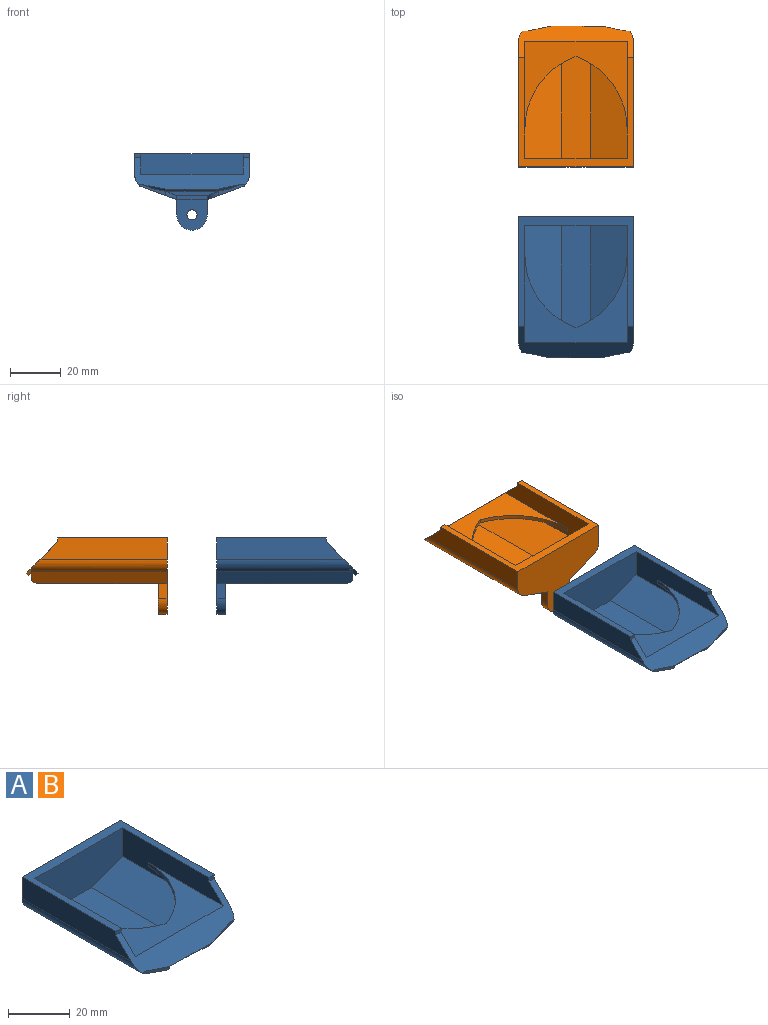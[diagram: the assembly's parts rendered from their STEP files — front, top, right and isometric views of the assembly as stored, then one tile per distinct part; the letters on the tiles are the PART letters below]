
ASSEMBLY  parts=2 mates=1
PART A: 43 faces, bbox 45x55.5x30 mm
  f0: plane 50x14.36mm, normal (-0.34,0,0.94), area 750.7mm2, adj f2,f6,f19,f21,f27,f30,f41
  f1: plane 50x14.36mm, normal (0.34,0,0.94), area 750.7mm2, adj f7,f8,f19,f21,f27,f31,f41
  f2: plane 10.49x4.33mm, normal (0,-1,0), area 12.7mm2, adj f0,f13,f26,f28,f30,f39,f41
  f3: plane 40.2x34.32mm, normal (0,0,1), area 549mm2, adj f6,f7,f22,f23,f26
  f4: plane 50x8.5mm, normal (1,0,0), area 389.9mm2, adj f14,f18,f24,f26,f28
  f5: plane 40.2x35.09mm, normal (0,0,-1), area 579.8mm2, adj f6,f7,f22,f23,f38
  f6: plane 47.58x11.28mm, normal (-1,0,0), area 437.8mm2, adj f0,f3,f5,f14,f21,f23,f24,f26
  f7: plane 47.58x11.28mm, normal (1,0,0), area 437.8mm2, adj f1,f3,f5,f14,f21,f22,f25,f26
  f8: plane 10.49x4.33mm, normal (0,-1,0), area 11.7mm2, adj f1,f17,f26,f29,f31,f40,f41
  f9: plane 12x12mm, normal (0,-1,0), area 116mm2, adj f10,f11,f12,f16,f20
  f10: plane 6x3.5mm, normal (-1,0,0), area 21mm2, adj f9,f11,f17,f18
  f11: cylinder r=6mm len=12mm, axis (0,1,0), area 66mm2, adj f9,f10,f12,f18
  f12: plane 6x3.5mm, normal (1,0,0), area 21mm2, adj f9,f11,f13,f18
  f13: plane 53.5x13.21mm, normal (0.34,0,-0.94), area 747.9mm2, adj f2,f12,f18,f20,f28,f30
  f14: plane 45x43mm, normal (0,0,1), area 347.1mm2, adj f4,f6,f7,f15,f18,f21,f24,f25
  f15: plane 50x8.5mm, normal (-1,0,0), area 389.9mm2, adj f14,f18,f25,f26,f29
  f16: cylinder r=2mm len=4mm, axis (0,1,0), area 44mm2, adj f9,f18
  f17: plane 53.5x13.21mm, normal (-0.34,0,-0.94), area 747.9mm2, adj f8,f10,f18,f20,f29,f31
  f18: plane 45x30mm, normal (0,1,0), area 822.5mm2, adj f4,f10,f11,f12,f13,f14,f15,f16
  f19: plane 47x11.47mm, normal (0,0,1), area 539.2mm2, adj f0,f1,f21,f27
  f20: plane 47x12mm, normal (0,0,-1), area 564mm2, adj f9,f13,f17,f27
  f21: plane 40.2x16.5mm, normal (0,-1,0), area 588.3mm2, adj f0,f1,f6,f7,f14,f19
  f22: cylinder r=30mm len=28.32mm, axis (0,0,1), area 55.6mm2, adj f3,f5,f7,f23
  f23: cylinder r=30mm len=28.32mm, axis (0,0,1), area 55.6mm2, adj f3,f5,f6,f22
  f24: plane 2.4x1.5mm, normal (0,-1,0), area 3.6mm2, adj f4,f6,f14,f26
  f25: plane 2.4x1.5mm, normal (0,-1,0), area 3.6mm2, adj f7,f14,f15,f26
  f26: plane 45x12.51mm, normal (0,-0.71,0.71), area 375mm2, adj f2,f3,f4,f6,f7,f8,f15,f24
  f27: plane 12x1.6mm, normal (0,-1,0), area 18mm2, adj f0,f1,f19,f20,f30,f31
  f28: cylinder r=5mm len=53.5mm, axis (0,1,0), area 320.4mm2, adj f2,f4,f13,f18,f26,f35,f36,f37
  f29: cylinder r=5mm len=53.5mm, axis (0,1,0), area 320.1mm2, adj f8,f15,f17,f18,f26,f32,f33,f34
  f30: cylinder r=5mm len=4.58mm, axis (0,0,1), area 9.3mm2, adj f0,f2,f13,f27
  f31: cylinder r=5mm len=4.58mm, axis (0,0,1), area 9.3mm2, adj f1,f8,f17,f27
  f32: plane 0.73x0.53mm, normal (0,0.71,-0.71), area 0.2mm2, adj f29,f33,f34
  f33: plane 0.73x0.53mm, normal (-0.27,-0.68,-0.68), area 0.2mm2, adj f29,f32,f34
  f34: plane 0.77x0.38mm, normal (-1,0,0), area 0.1mm2, adj f29,f32,f33
  f35: plane 0.2x0.15mm, normal (0,0.71,-0.71), area 0mm2, adj f28,f36,f37
  f36: plane 0.22x0.11mm, normal (1,0,0), area 0mm2, adj f28,f35,f37
  f37: plane 0.2x0.15mm, normal (0.29,-0.68,-0.68), area 0mm2, adj f28,f35,f36
  f38: plane 40.2x0.48mm, normal (0,0.71,0.71), area 27.4mm2, adj f5,f6,f7,f41
  f39: plane 9.44x2.86mm, normal (0.29,-0.68,-0.68), area 9.3mm2, adj f2,f26,f41,f42
  f40: plane 9.43x2.73mm, normal (-0.27,-0.68,-0.68), area 9.1mm2, adj f8,f26,f41,f42
  f41: plane 40.2x4.87mm, normal (0,0.71,-0.71), area 227.5mm2, adj f0,f1,f2,f6,f7,f8,f38,f39
  f42: plane 19.95x0.98mm, normal (-0.01,-0.71,-0.71), area 23.9mm2, adj f26,f39,f40,f41
PART B: same geometry as A
PLACE A t=(12.71,0,-6.99)mm
PLACE B rot(axis=(0,0,1),180deg) t=(12.71,19.64,-6.99)mm
MATE slider B.f11 <-> A.f11  axis (0,-1,0) through (12.71,23.14,-30.99)mm
